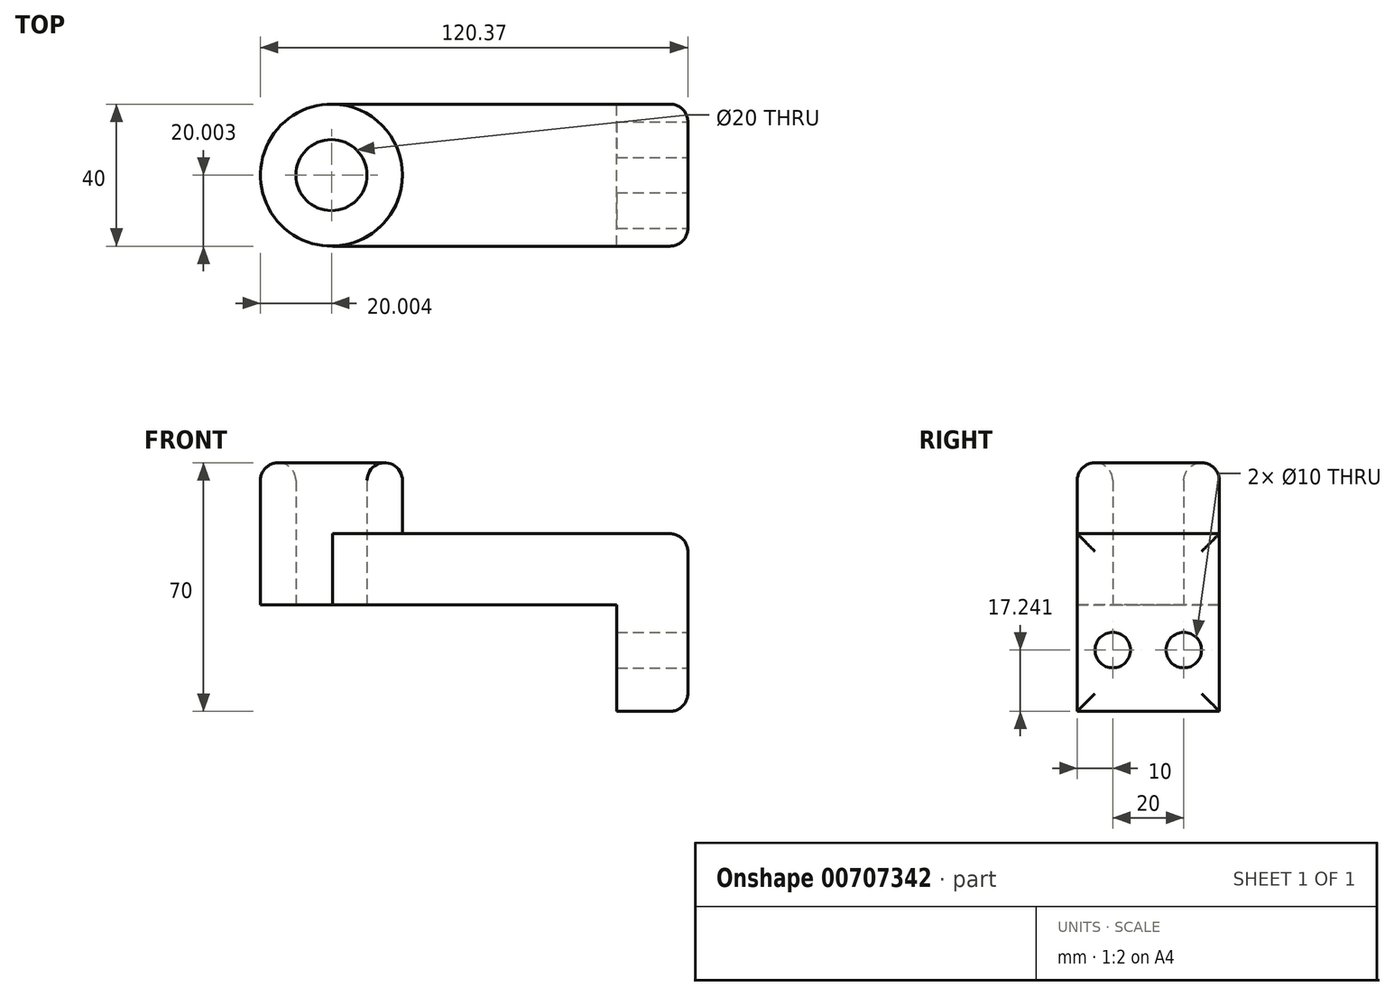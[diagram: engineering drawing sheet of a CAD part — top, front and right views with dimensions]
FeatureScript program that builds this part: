
annotation { "Feature Type Name" : "Feature", "Feature Type Description" : "" }
export const myFeature = defineFeature(function(context is Context, id is Id, definition is map)
    precondition{}
    {
        {
            var Q0;
            Q0=qCreatedBy(makeId("Top.planeOp"),FACE);
            var sketch = newSketch(context, id + "F0", { "sketchPlane" : qUnion([Q0])});
            skCircle(sketch, "E0", {"center": v(-56.68, 20) * mm, "radius": 20 * mm});
            skLineSegment(sketch, "E1.bottom", {"start": v(-56.31, 40) * mm, "end": v(43.69, 40) * mm});
            skLineSegment(sketch, "E1.top", {"start": v(-56.31, 0) * mm, "end": v(43.69, 0) * mm});
            skLineSegment(sketch, "E1.left", {"start": v(-56.31, 0) * mm, "end": v(-56.31, 0) * mm});
            skLineSegment(sketch, "E1.right", {"start": v(43.69, 40) * mm, "end": v(43.69, 0) * mm});
            skCircle(sketch, "E2", {"center": v(-56.68, 20) * mm, "radius": 10 * mm});
            skSolve(sketch);
        }
        {
            var Q0;
            {var subQ0=sQuery(id+"F0.wireOp",EDGE,"E0");var subQ1=makeQuery(id+"F0.imprint","INTERSECT",VERTEX,{"derivedFrom":[subQ0,sQuery(id+"F0.wireOp",EDGE,"E1.bottom")]});Q0=makeQuery(id+"F0.imprint","IMPRINT",FACE,{"disambiguationData":[TD([[makeQuery(id+"F0.imprint","IMPRINT",EDGE,{"disambiguationData":[TD([[subQ1,-1.0]])],"derivedFrom":subQ0}),1.0]])]});}
            extrude(context, id + "F1", {"entities" : qUnion([Q0]), "depth" : 40 * mm, "offsetDistance" : 25 * mm});
        }
        {
            var Q0;
            {var subQ1=sQuery(id+"F0.wireOp",EDGE,"E1.bottom");Q0=makeQuery(id+"F0.imprint","IMPRINT",FACE,{"disambiguationData":[TD([[makeQuery(id+"F0.imprint","IMPRINT",EDGE,{"derivedFrom":subQ1}),-1.0]])]});}
            extrude(context, id + "F2", {"entities" : qUnion([Q0]), "operationType" : NewBodyOperationType.ADD, "depth" : 20 * mm, "offsetDistance" : 25 * mm});
        }
        {
            var Q0;
            {var subQ1=sQuery(id+"F0.wireOp",EDGE,"E1.bottom");Q0=makeQuery(id+"F0.imprint","IMPRINT",FACE,{"disambiguationData":[TD([[makeQuery(id+"F0.imprint","IMPRINT",EDGE,{"derivedFrom":subQ1}),-1.0]])]});}
            var sketch = newSketch(context, id + "F3", { "sketchPlane" : qUnion([Q0])});
            skLineSegment(sketch, "E3.bottom", {"start": v(43.69, 0) * mm, "end": v(23.69, 0) * mm});
            skLineSegment(sketch, "E3.top", {"start": v(43.69, 40) * mm, "end": v(23.69, 40) * mm});
            skLineSegment(sketch, "E3.left", {"start": v(43.69, 0) * mm, "end": v(43.69, 40) * mm});
            skLineSegment(sketch, "E3.right", {"start": v(23.69, 0) * mm, "end": v(23.69, 40) * mm});
            skSolve(sketch);
        }
        {
            var Q0;
            Q0=makeQuery(id+"F3.imprint","IMPRINT",FACE,{"disambiguationData":[TD([[makeQuery(id+"F3.imprint","IMPRINT",EDGE,{"derivedFrom":sQuery(id+"F3.wireOp",EDGE,"E3.bottom")}),1.0]])]});
            extrude(context, id + "F4", {"entities" : qUnion([Q0]), "operationType" : NewBodyOperationType.ADD, "oppositeDirection" : true, "depth" : 30 * mm, "offsetDistance" : 25 * mm});
        }
        {
            var Q0;
            Q0=makeQuery(id+"F4.boolean.opBoolean","MERGE",FACE,{"derivedFrom":[makeQuery(id+"F2.opExtrude","SWEPT_FACE",FACE,{"disambiguationData":[OSD([sQuery(id+"F0.wireOp",EDGE,"E1.right")])]}),makeQuery(id+"F4.opExtrude","SWEPT_FACE",FACE,{"disambiguationData":[OSD([sQuery(id+"F3.wireOp",EDGE,"E3.left")])]})]});
            var sketch = newSketch(context, id + "F5", { "sketchPlane" : qUnion([Q0])});
            skCircle(sketch, "E4", {"center": v(10, -12.76) * mm, "radius": 5 * mm});
            skCircle(sketch, "E5", {"center": v(30, -12.76) * mm, "radius": 5 * mm});
            skSolve(sketch);
        }
        {
            var Q0;
            Q0=makeQuery(id+"F5.imprint","IMPRINT",FACE,{"disambiguationData":[TD([[makeQuery(id+"F5.imprint","IMPRINT",EDGE,{"derivedFrom":sQuery(id+"F5.wireOp",EDGE,"E4")}),1.0]])]});
            var Q1;
            Q1=makeQuery(id+"F5.imprint","IMPRINT",FACE,{"disambiguationData":[TD([[makeQuery(id+"F5.imprint","IMPRINT",EDGE,{"derivedFrom":sQuery(id+"F5.wireOp",EDGE,"E5")}),1.0]])]});
            extrude(context, id + "F6", {"entities" : qUnion([Q0, Q1]), "operationType" : NewBodyOperationType.REMOVE, "endBound" : BoundingType.UP_TO_NEXT, "oppositeDirection" : true, "depth" : 25 * mm, "offsetDistance" : 25 * mm});
        }
        {
            var Q0;
            Q0=makeQuery(id+"F1.opExtrude","CAP_FACE",FACE,{"disambiguationData":[OSD([sQuery(id+"F0.wireOp",EDGE,"E0"),sQuery(id+"F0.wireOp",EDGE,"E2")])],"isStart":false});
            var Q1;
            Q1=makeQuery(id+"F2.opExtrude","CAP_EDGE",EDGE,{"disambiguationData":[OSD([sQuery(id+"F0.wireOp",EDGE,"E0")])],"isStart":false});
            var Q2;
            Q2=makeQuery(id+"F2.opExtrude","CAP_EDGE",EDGE,{"disambiguationData":[OSD([sQuery(id+"F0.wireOp",EDGE,"E1.right")])],"isStart":false});
            var Q3;
            Q3=makeQuery(id+"F4.boolean.opBoolean","MERGE",EDGE,{"derivedFrom":[makeQuery(id+"F2.opExtrude","SWEPT_EDGE",EDGE,{"disambiguationData":[OSD([sQuery(id+"F0.wireOp",EDGE,"E1.bottom"),sQuery(id+"F0.wireOp",EDGE,"E1.right")])]}),makeQuery(id+"F4.opExtrude","SWEPT_EDGE",EDGE,{"disambiguationData":[OSD([sQuery(id+"F3.wireOp",EDGE,"E3.top"),sQuery(id+"F3.wireOp",EDGE,"E3.left")])]})]});
            var Q4;
            Q4=makeQuery(id+"F4.boolean.opBoolean","MERGE",EDGE,{"derivedFrom":[makeQuery(id+"F2.opExtrude","SWEPT_EDGE",EDGE,{"disambiguationData":[OSD([sQuery(id+"F0.wireOp",EDGE,"E1.top"),sQuery(id+"F0.wireOp",EDGE,"E1.right")])]}),makeQuery(id+"F4.opExtrude","SWEPT_EDGE",EDGE,{"disambiguationData":[OSD([sQuery(id+"F3.wireOp",EDGE,"E3.bottom"),sQuery(id+"F3.wireOp",EDGE,"E3.left")])]})]});
            var Q5;
            Q5=makeQuery(id+"F4.opExtrude","CAP_EDGE",EDGE,{"disambiguationData":[OSD([sQuery(id+"F3.wireOp",EDGE,"E3.left")])],"isStart":false});
            fillet(context, id + "F7", {"entities" : qUnion([Q0, Q1, Q2, Q3, Q4, Q5]), "radius" : 5 * mm, "tangentPropagation" : true, "allowEdgeOverflow" : false});
        }
    });
